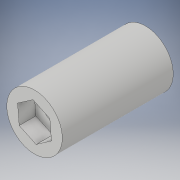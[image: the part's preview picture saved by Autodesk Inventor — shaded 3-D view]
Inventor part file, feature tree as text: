
AUTODESK INVENTOR PART (.ipt)
format: ipt  version: 2017 (Build 210142000, 142)  size: 121,856 bytes
history: native  units: in
note: dims shown in document units (in); Inventor stores cm internally (conversion verified against a paired STEP export)
features: sketch x6, extrude x3, hole x1
ambient origin geometry x8: Origin, YZ Plane, XZ Plane, XY Plane, X Axis, Y Axis, Z Axis, Center Point
bodies: Body1 (feature_tree)
feature tree (10):
  extrude  "Extrusion3"  Depth=0.75in TaperAngle=0.0deg
  extrude  "Extrusion4"  Depth=0.225in TaperAngle=0.0deg
  hole  "Hole1"  [1 undecoded]
  sketch  "Sketch6"  dims[d14=0.187in d15=0.75in d16=0.375in d17=0.25in d18=0.5635in d19=0.525in d20=0.8108in d21=0.2in]
  sketch  "Sketch7"  dims[d28=0.75in d29=0.0in]
  extrude  "Extrusion5"  [1 undecoded]
  sketch  "Sketch3"  dims[d7=0.75in d8=1.5in d9=0.0in]
  sketch  "Sketch4"  dims[d10=0.4375in d11=0.225in d12=0.0in]
  sketch  "Sketch5"  dims[d13=0.187in]
  sketch  "Sketch8"
note: 2 required parameter values undecoded (feature->parameter linkage not recoverable at this tier; creation-order binding heuristic only, values carry confidence <= 0.55)
